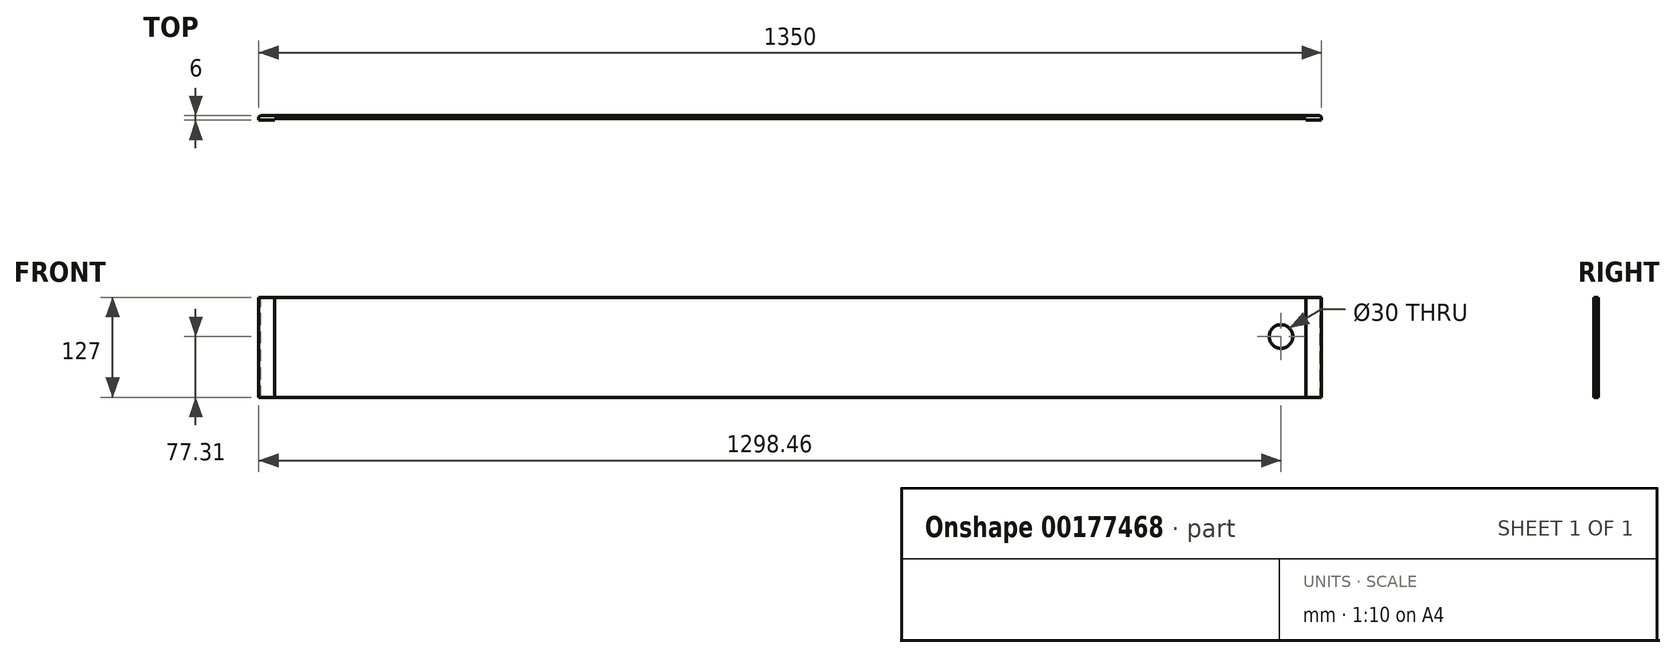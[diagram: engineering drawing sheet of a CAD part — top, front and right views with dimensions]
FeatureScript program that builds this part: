
annotation { "Feature Type Name" : "Feature", "Feature Type Description" : "" }
export const myFeature = defineFeature(function(context is Context, id is Id, definition is map)
    precondition{}
    {
        {
            var Q0;
            Q0=qCreatedBy(makeId("Front.planeOp"),FACE);
            var sketch = newSketch(context, id + "F0", { "sketchPlane" : qUnion([Q0])});
            skLineSegment(sketch, "E0.bottom", {"start": v(675, -63.5) * mm, "end": v(-675, -63.5) * mm});
            skLineSegment(sketch, "E0.top", {"start": v(675, 63.5) * mm, "end": v(-675, 63.5) * mm});
            skLineSegment(sketch, "E0.left", {"start": v(675, -63.5) * mm, "end": v(675, 63.5) * mm});
            skLineSegment(sketch, "E0.right", {"start": v(-675, -63.5) * mm, "end": v(-675, 63.5) * mm});
            skPoint(sketch, "E0.middle", {"position": v(0, 0) * mm});
            skPoint(sketch, "E1", {"position": v(623.46, 13.81) * mm});
            skLineSegment(sketch, "E2.0", {"start": v(-655, -63.5) * mm, "end": v(-655, 63.5) * mm});
            skLineSegment(sketch, "E3.0", {"start": v(655, -63.5) * mm, "end": v(655, 63.5) * mm});
            skSolve(sketch);
        }
        {
            var Q0;
            {var subQ0=sQuery(id+"F0.wireOp",EDGE,"E0.right");Q0=makeQuery(id+"F0.imprint","IMPRINT",FACE,{"disambiguationData":[TD([[makeQuery(id+"F0.imprint","IMPRINT",EDGE,{"derivedFrom":subQ0}),-1.0]])]});}
            var Q1;
            {var subQ0=sQuery(id+"F0.wireOp",EDGE,"E2.0");Q1=makeQuery(id+"F0.imprint","IMPRINT",FACE,{"disambiguationData":[TD([[makeQuery(id+"F0.imprint","IMPRINT",EDGE,{"derivedFrom":subQ0}),-1.0]])]});}
            var Q2;
            {var subQ0=sQuery(id+"F0.wireOp",EDGE,"E0.left");Q2=makeQuery(id+"F0.imprint","IMPRINT",FACE,{"disambiguationData":[TD([[makeQuery(id+"F0.imprint","IMPRINT",EDGE,{"derivedFrom":subQ0}),1.0]])]});}
            extrude(context, id + "F1", {"entities" : qUnion([Q0, Q1, Q2]), "depth" : 4 * mm});
        }
        {
            var Q0;
            Q0=sQuery(id+"F0.wireOp",VERTEX,"E1");
            var Q1;
            Q1=makeQuery(id+"F1.opExtrude","SWEPT_BODY",BODY,{"disambiguationData":[OSD([sQuery(id+"F0.wireOp",EDGE,"E0.bottom"),sQuery(id+"F0.wireOp",EDGE,"E0.top"),sQuery(id+"F0.wireOp",EDGE,"E0.right"),sQuery(id+"F0.wireOp",EDGE,"E3.0")])]});
            hole(context, id + "F2", {"style" : HoleStyle.SIMPLE, "endStyle" : HoleEndStyle.THROUGH, "oppositeDirection" : true, "holeDiameter" : 30 * mm, "locations" : qUnion([Q0]), "scope" : qUnion([Q1]), "isTappedThrough" : true});
        }
        {
            var Q0;
            Q0=makeQuery(id+"F1.opExtrude","CAP_FACE",FACE,{"disambiguationData":[OSD([sQuery(id+"F0.wireOp",EDGE,"E0.bottom"),sQuery(id+"F0.wireOp",EDGE,"E0.top"),sQuery(id+"F0.wireOp",EDGE,"E0.left"),sQuery(id+"F0.wireOp",EDGE,"E0.right")])],"isStart":false});
            var sketch = newSketch(context, id + "F3", { "sketchPlane" : qUnion([Q0])});
            skLineSegment(sketch, "E4.0", {"start": v(655, -63.5) * mm, "end": v(655, 63.5) * mm});
            skLineSegment(sketch, "E5.0", {"start": v(-655, -63.5) * mm, "end": v(-655, 63.5) * mm});
            skSolve(sketch);
        }
        {
            var Q0;
            {var subQ0=sQuery(id+"F3.wireOp",EDGE,"E5.0");Q0=makeQuery(id+"F3.imprint","IMPRINT",FACE,{"disambiguationData":[TD([[makeQuery(id+"F3.imprint","IMPRINT",EDGE,{"derivedFrom":subQ0}),1.0]])]});}
            var Q1;
            {var subQ0=sQuery(id+"F3.wireOp",EDGE,"E4.0");Q1=makeQuery(id+"F3.imprint","IMPRINT",FACE,{"disambiguationData":[TD([[makeQuery(id+"F3.imprint","IMPRINT",EDGE,{"derivedFrom":subQ0}),-1.0]])]});}
            extrude(context, id + "F4", {"entities" : qUnion([Q0, Q1]), "operationType" : NewBodyOperationType.ADD, "depth" : 2 * mm});
        }
        {
            var Q0;
            Q0=makeQuery(id+"F1.opExtrude","CAP_EDGE",EDGE,{"disambiguationData":[OSD([sQuery(id+"F0.wireOp",EDGE,"E0.left")])],"isStart":true});
            var Q1;
            Q1=makeQuery(id+"F1.opExtrude","CAP_EDGE",EDGE,{"disambiguationData":[OSD([sQuery(id+"F0.wireOp",EDGE,"E0.right")])],"isStart":true});
            chamfer(context, id + "F5", {"entities" : qUnion([Q0, Q1]), "width" : 2 * mm, "tangentPropagation" : true});
        }
    });
